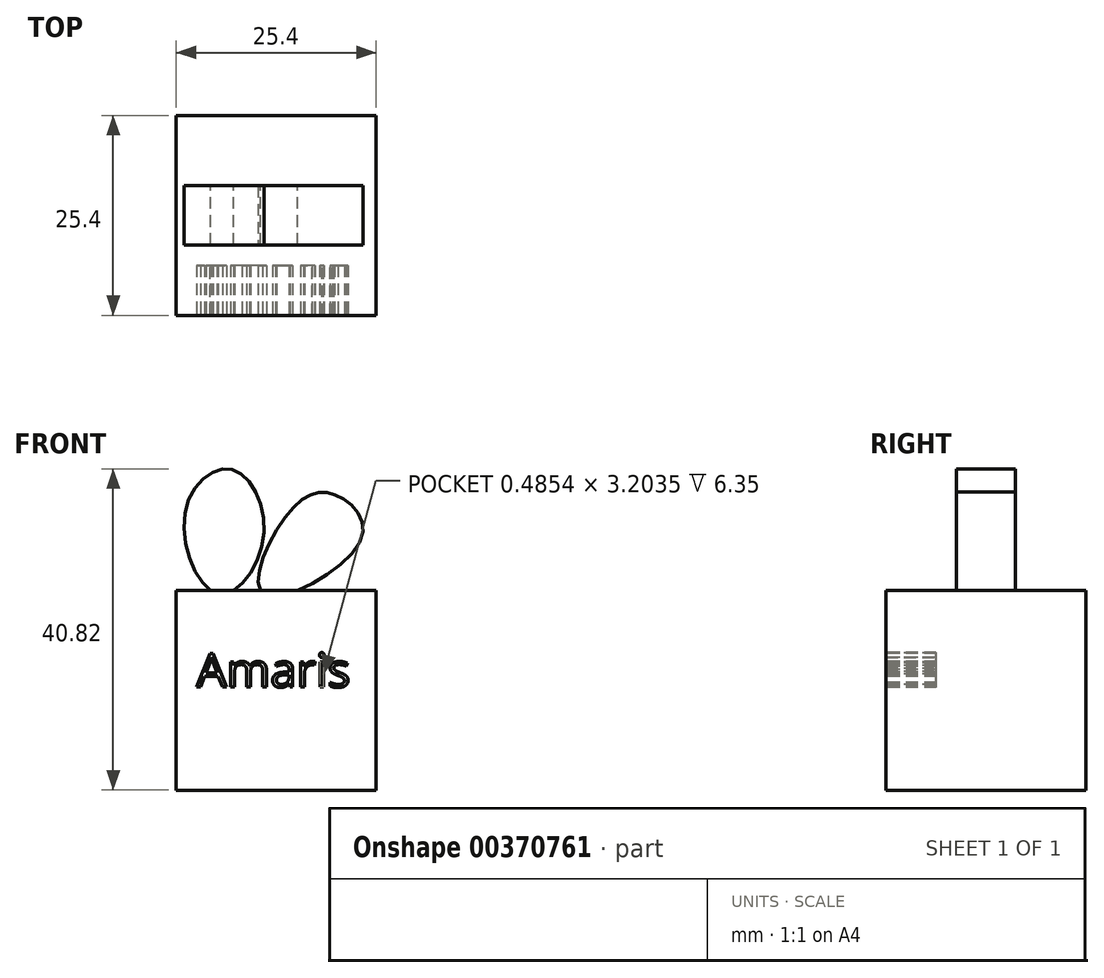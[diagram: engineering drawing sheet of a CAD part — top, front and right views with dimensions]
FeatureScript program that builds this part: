
annotation { "Feature Type Name" : "Feature", "Feature Type Description" : "" }
export const myFeature = defineFeature(function(context is Context, id is Id, definition is map)
    precondition{}
    {
        {
            var Q0;
            Q0=qCreatedBy(makeId("Front.planeOp"),FACE);
            var sketch = newSketch(context, id + "F0", { "sketchPlane" : qUnion([Q0])});
            skLineSegment(sketch, "E0.bottom", {"start": v(-44.56, 9.38) * mm, "end": v(-19.16, 9.38) * mm});
            skLineSegment(sketch, "E0.top", {"start": v(-44.56, 34.78) * mm, "end": v(-19.16, 34.78) * mm});
            skLineSegment(sketch, "E0.left", {"start": v(-44.56, 9.38) * mm, "end": v(-44.56, 34.78) * mm});
            skLineSegment(sketch, "E0.right", {"start": v(-19.16, 9.38) * mm, "end": v(-19.16, 34.78) * mm});
            skSolve(sketch);
        }
        {
            var Q0;
            Q0 = qSketchRegion(id + "F0", true);
            extrude(context, id + "F1", {"entities" : qUnion([Q0]), "endBound" : BoundingType.SYMMETRIC, "depth" : 25.4 * mm});
        }
        {
            var Q0;
            Q0=qCreatedBy(makeId("Front.planeOp"),FACE);
            cPlane(context, id + "F2", {"entities" : qUnion([Q0]), "cplaneType" : CPlaneType.OFFSET, "offset" : 0 * mm, "width" : 152.4 * mm, "height" : 152.4 * mm});
        }
        {
            var Q0;
            Q0=qCreatedBy(makeId("Front.planeOp"),FACE);
            var sketch = newSketch(context, id + "F3", { "sketchPlane" : qUnion([Q0])});
            skFitSpline(sketch, "E1", {"points": [v(-39.27, 34.37) * mm, v(-43.4, 44.87) * mm, v(-37.44, 50.1) * mm, v(-33.52, 41.22) * mm, v(-39.27, 34.37) * mm]});
            skFitSpline(sketch, "E2", {"points": [v(-33.47, 34.37) * mm, v(-29.81, 45.14) * mm, v(-24.19, 46.82) * mm, v(-21.1, 41.22) * mm, v(-33.47, 34.37) * mm]});
            skFitSpline(sketch, "E3.0", {"points": [v(-38.8, 34.74) * mm, v(-39.17, 34.79) * mm, v(-39.55, 34.9) * mm, v(-40.07, 35.2) * mm, v(-40.72, 35.75) * mm, v(-41.45, 36.73) * mm, v(-42.3, 38.33) * mm, v(-42.9, 40.27) * mm, v(-43.16, 42.28) * mm, v(-43.15, 43.76) * mm, v(-42.93, 45.14) * mm, v(-42.5, 46.39) * mm, v(-41.87, 47.48) * mm, v(-41.1, 48.4) * mm, v(-40.25, 49.1) * mm, v(-39.35, 49.57) * mm, v(-38.46, 49.79) * mm, v(-37.75, 49.75) * mm, v(-37.21, 49.58) * mm, v(-36.68, 49.32) * mm, v(-36.04, 48.83) * mm, v(-35.35, 47.98) * mm, v(-34.55, 46.58) * mm, v(-34.02, 44.85) * mm, v(-33.83, 43) * mm, v(-33.88, 41.57) * mm, v(-34.14, 40.17) * mm, v(-34.59, 38.82) * mm, v(-35.2, 37.59) * mm, v(-35.93, 36.5) * mm, v(-36.74, 35.64) * mm, v(-37.58, 35.04) * mm, v(-38.27, 34.8) * mm, v(-38.8, 34.74) * mm, v(-39.17, 34.79) * mm, v(-39.55, 34.9) * mm, v(-38.8, 34.74) * mm]});
            skFitSpline(sketch, "E4.0", {"points": [v(-32.95, 34.6) * mm, v(-33.23, 34.73) * mm, v(-33.42, 34.91) * mm, v(-33.57, 35.17) * mm, v(-33.66, 35.53) * mm, v(-33.72, 36.12) * mm, v(-33.62, 37.04) * mm, v(-33.26, 38.35) * mm, v(-32.7, 39.76) * mm, v(-32, 41.2) * mm, v(-31.18, 42.6) * mm, v(-30.3, 43.87) * mm, v(-29.4, 44.95) * mm, v(-28.56, 45.76) * mm, v(-27.75, 46.33) * mm, v(-26.97, 46.67) * mm, v(-26.21, 46.8) * mm, v(-25.45, 46.77) * mm, v(-24.65, 46.56) * mm, v(-23.81, 46.17) * mm, v(-23, 45.63) * mm, v(-22.26, 44.95) * mm, v(-21.68, 44.17) * mm, v(-21.32, 43.32) * mm, v(-21.24, 42.57) * mm, v(-21.32, 41.93) * mm, v(-21.47, 41.44) * mm, v(-21.72, 40.91) * mm, v(-22.18, 40.19) * mm, v(-22.99, 39.25) * mm, v(-24.22, 38.14) * mm, v(-25.65, 37.1) * mm, v(-27.18, 36.17) * mm, v(-28.73, 35.4) * mm, v(-30.22, 34.83) * mm, v(-31.33, 34.57) * mm, v(-32.08, 34.5) * mm, v(-32.57, 34.51) * mm, v(-32.95, 34.6) * mm, v(-33.23, 34.73) * mm, v(-33.42, 34.91) * mm, v(-32.95, 34.6) * mm]});
            skSolve(sketch);
        }
        {
            var Q0;
            Q0 = qSketchRegion(id + "F3", true);
            extrude(context, id + "F4", {"entities" : qUnion([Q0]), "operationType" : NewBodyOperationType.ADD, "endBound" : BoundingType.SYMMETRIC, "depth" : 7.52 * mm});
        }
        {
            var Q0;
            Q0=makeQuery(id+"F1.opExtrude","CAP_FACE",FACE,{"disambiguationData":[OSD([sQuery(id+"F0.wireOp",EDGE,"E0.bottom"),sQuery(id+"F0.wireOp",EDGE,"E0.top"),sQuery(id+"F0.wireOp",EDGE,"E0.left"),sQuery(id+"F0.wireOp",EDGE,"E0.right")])],"isStart":false});
            var sketch = newSketch(context, id + "F5", { "sketchPlane" : qUnion([Q0])});
            skText(sketch, "E5", { "text": "Amaris\n", "fontName": "OpenSans-Regular.ttf"});
            const initialGuessF5  = {"E5": [-0.04196, 0.02247, 1, 0, 0.00431]};
            skSetInitialGuess(sketch, initialGuessF5);
            skSolve(sketch);
        }
        {
            var Q0;
            Q0 = qSketchRegion(id + "F5", true);
            extrude(context, id + "F6", {"entities" : qUnion([Q0]), "operationType" : NewBodyOperationType.REMOVE, "oppositeDirection" : true, "depth" : 6.35 * mm});
        }
    });
